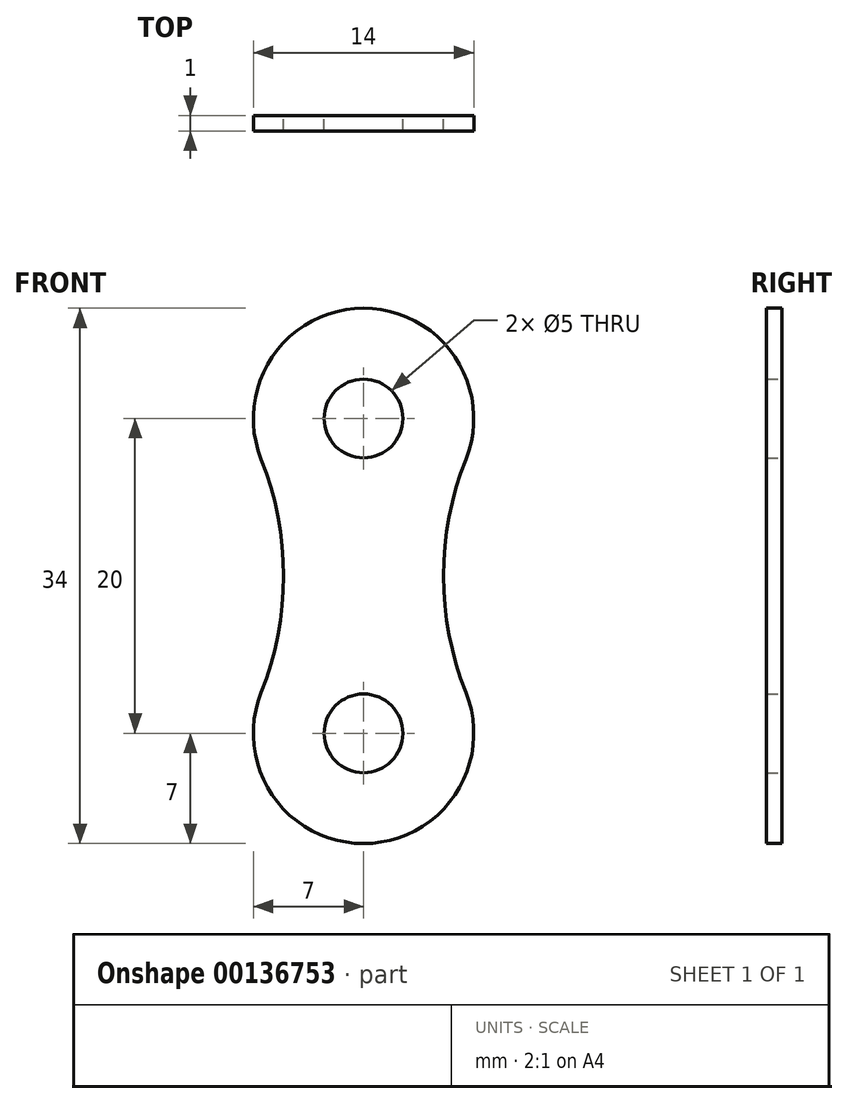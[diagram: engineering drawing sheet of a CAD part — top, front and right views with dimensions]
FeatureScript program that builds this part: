
annotation { "Feature Type Name" : "Feature", "Feature Type Description" : "" }
export const myFeature = defineFeature(function(context is Context, id is Id, definition is map)
    precondition{}
    {
        {
            var Q0;
            Q0=qCreatedBy(makeId("Front.planeOp"),FACE);
            var sketch = newSketch(context, id + "F0", { "sketchPlane" : qUnion([Q0])});
            skArc(sketch, "E0", {"start": v(6.5, 7.4) * mm, "mid": v(0, 17) * mm, "end": v(-6.5, 7.4) * mm});
            skArc(sketch, "E1", {"start": v(-6.5, -7.4) * mm, "mid": v(0, -17) * mm, "end": v(6.5, -7.4) * mm});
            skArc(sketch, "E2", {"start": v(-6.5, -7.4) * mm, "mid": v(-5.08, 0) * mm, "end": v(-6.5, 7.4) * mm});
            skArc(sketch, "E3", {"start": v(6.5, 7.4) * mm, "mid": v(5.08, 0) * mm, "end": v(6.5, -7.4) * mm});
            skCircle(sketch, "E4", {"center": v(0, 10) * mm, "radius": 2.5 * mm});
            skCircle(sketch, "E5", {"center": v(0, -10) * mm, "radius": 2.5 * mm});
            skSolve(sketch);
        }
        {
            var Q0;
            Q0=makeQuery(id+"F0.imprint","IMPRINT",FACE,{"disambiguationData":[TD([[makeQuery(id+"F0.imprint","IMPRINT",EDGE,{"derivedFrom":sQuery(id+"F0.wireOp",EDGE,"E0")}),1.0]])]});
            extrude(context, id + "F1", {"entities" : qUnion([Q0]), "depth" : 1 * mm});
        }
    });
